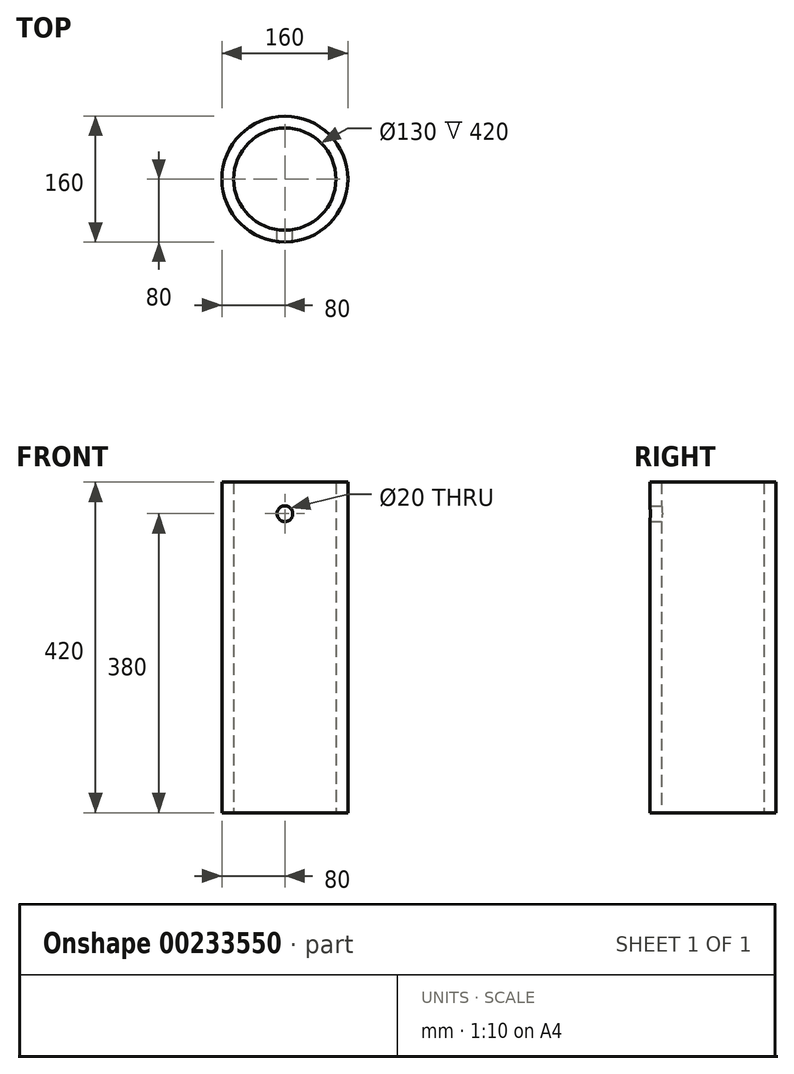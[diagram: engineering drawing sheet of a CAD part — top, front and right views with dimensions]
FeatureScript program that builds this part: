
annotation { "Feature Type Name" : "Feature", "Feature Type Description" : "" }
export const myFeature = defineFeature(function(context is Context, id is Id, definition is map)
    precondition{}
    {
        {
            var Q0;
            Q0=qCreatedBy(makeId("Top.planeOp"),FACE);
            var sketch = newSketch(context, id + "F0", { "sketchPlane" : qUnion([Q0])});
            skCircle(sketch, "E0", {"center": v(0, 0) * mm, "radius": 80 * mm});
            skCircle(sketch, "E1", {"center": v(0, 0) * mm, "radius": 65 * mm});
            skSolve(sketch);
        }
        {
            var Q0;
            Q0=makeQuery(id+"F0.imprint","IMPRINT",FACE,{"disambiguationData":[TD([[makeQuery(id+"F0.imprint","IMPRINT",EDGE,{"derivedFrom":sQuery(id+"F0.wireOp",EDGE,"E0")}),1.0]])]});
            extrude(context, id + "F1", {"entities" : qUnion([Q0]), "endBound" : BoundingType.SYMMETRIC, "depth" : 420 * mm});
        }
        {
            var Q0;
            Q0=qCreatedBy(makeId("Front.planeOp"),FACE);
            var sketch = newSketch(context, id + "F2", { "sketchPlane" : qUnion([Q0])});
            skCircle(sketch, "E2", {"center": v(0, 170) * mm, "radius": 10 * mm});
            skSolve(sketch);
        }
        {
            var Q0;
            Q0 = qSketchRegion(id + "F2", true);
            extrude(context, id + "F3", {"entities" : qUnion([Q0]), "operationType" : NewBodyOperationType.REMOVE, "endBound" : BoundingType.THROUGH_ALL, "depth" : 25 * mm});
        }
    });
